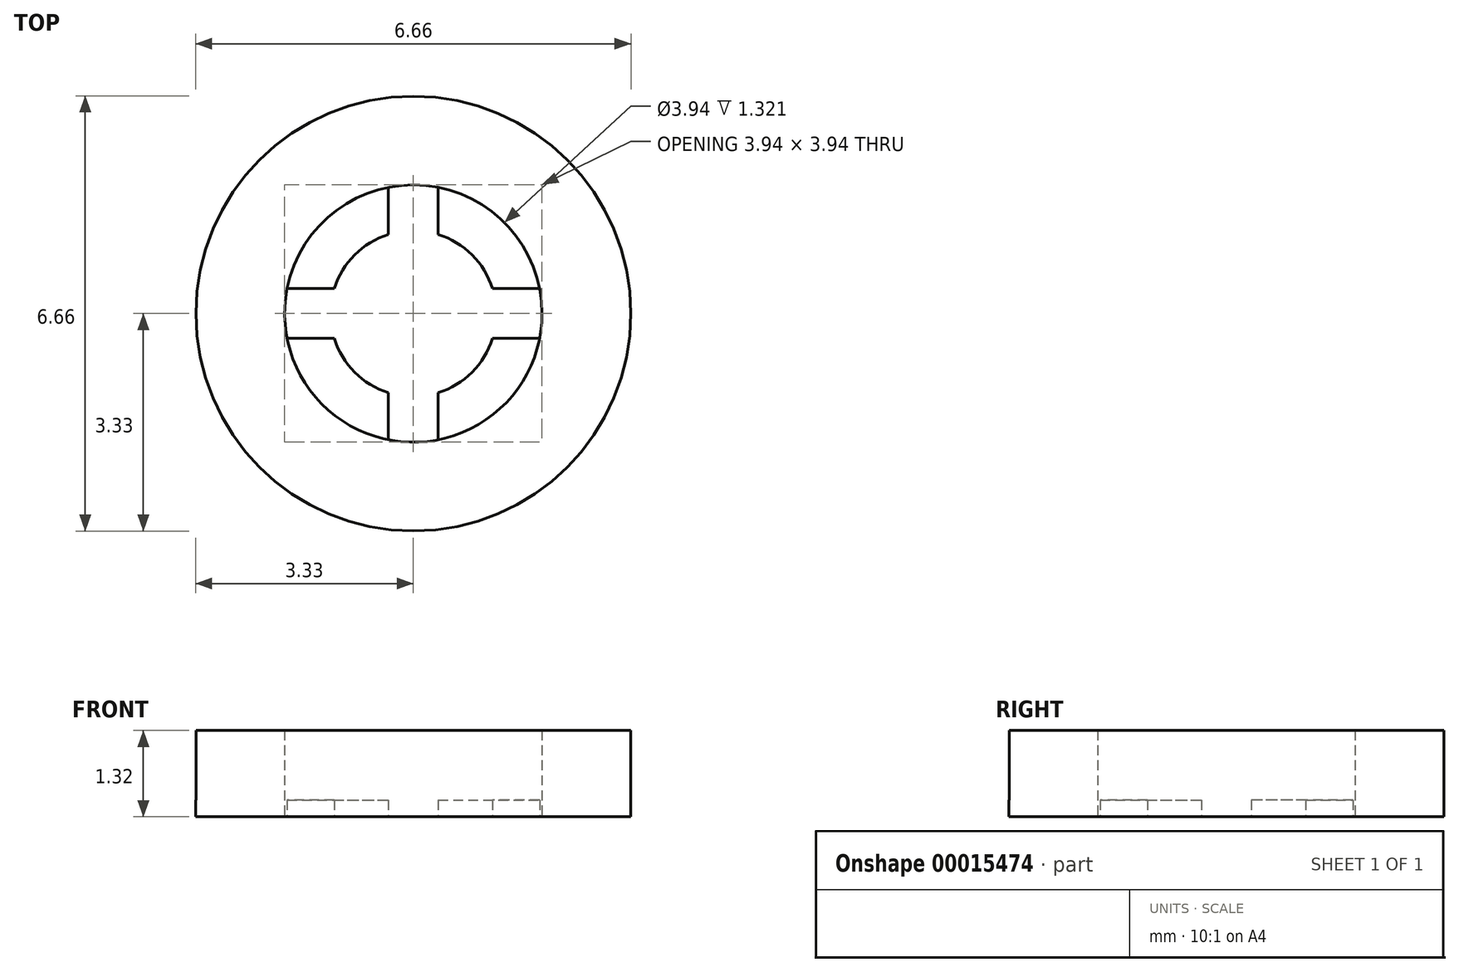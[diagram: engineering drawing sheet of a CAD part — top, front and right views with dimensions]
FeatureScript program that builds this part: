
annotation { "Feature Type Name" : "Feature", "Feature Type Description" : "" }
export const myFeature = defineFeature(function(context is Context, id is Id, definition is map)
    precondition{}
    {
        {
            var Q0;
            Q0=qCreatedBy(makeId("Top.planeOp"),FACE);
            var sketch = newSketch(context, id + "F0", { "sketchPlane" : qUnion([Q0])});
            skCircle(sketch, "E0", {"center": v(0, 0) * mm, "radius": 3.33 * mm});
            skArc(sketch, "E1", {"start": v(-1.93, 0.38) * mm, "mid": v(-1.97, 0) * mm, "end": v(-1.93, -0.38) * mm});
            skLineSegment(sketch, "E2", {"start": v(-1.97, 0) * mm, "end": v(1.97, 0) * mm, "construction": true});
            skLineSegment(sketch, "E3", {"start": v(0, 1.27) * mm, "end": v(0, -1.97) * mm, "construction": true});
            skArc(sketch, "E4", {"start": v(-0.38, 1.21) * mm, "mid": v(-0.9, 0.9) * mm, "end": v(-1.21, 0.38) * mm});
            skLineSegment(sketch, "E5", {"start": v(0.38, 1.93) * mm, "end": v(0.38, 1.21) * mm});
            skLineSegment(sketch, "E6", {"start": v(-0.38, -1.93) * mm, "end": v(-0.38, -1.21) * mm});
            skLineSegment(sketch, "E7", {"start": v(-1.93, 0.38) * mm, "end": v(-1.21, 0.38) * mm});
            skLineSegment(sketch, "E8", {"start": v(1.93, -0.38) * mm, "end": v(1.21, -0.38) * mm});
            skPoint(sketch, "E9.orphan", {"position": v(0, 1.97) * mm});
            skLineSegment(sketch, "E10.trimOffspring", {"start": v(1.21, 0.38) * mm, "end": v(1.93, 0.38) * mm});
            skLineSegment(sketch, "E11.trimOffspring", {"start": v(-0.38, 1.21) * mm, "end": v(-0.38, 1.93) * mm});
            skLineSegment(sketch, "E12.trimOffspring", {"start": v(0.38, -1.21) * mm, "end": v(0.38, -1.93) * mm});
            skArc(sketch, "E13.trimOffspring", {"start": v(1.21, 0.38) * mm, "mid": v(0.9, 0.9) * mm, "end": v(0.38, 1.21) * mm});
            skArc(sketch, "E14.trimOffspring", {"start": v(0.38, -1.21) * mm, "mid": v(0.9, -0.9) * mm, "end": v(1.21, -0.38) * mm});
            skArc(sketch, "E15.trimOffspring", {"start": v(-1.21, -0.38) * mm, "mid": v(-0.9, -0.9) * mm, "end": v(-0.38, -1.21) * mm});
            skLineSegment(sketch, "E16.trimOffspring", {"start": v(-1.21, -0.38) * mm, "end": v(-1.93, -0.38) * mm});
            skArc(sketch, "E17.trimOffspring", {"start": v(0.38, 1.93) * mm, "mid": v(0, 1.97) * mm, "end": v(-0.38, 1.93) * mm});
            skArc(sketch, "E18.trimOffspring", {"start": v(1.93, -0.38) * mm, "mid": v(1.97, 0) * mm, "end": v(1.93, 0.38) * mm});
            skArc(sketch, "E19.trimOffspring", {"start": v(-0.38, -1.93) * mm, "mid": v(0, -1.97) * mm, "end": v(0.38, -1.93) * mm});
            skSolve(sketch);
        }
        {
            var Q0;
            Q0=qSketchRegion(id+"F0",true);
            extrude(context, id + "F1", {"entities" : qUnion([Q0]), "depth" : 0.25 * mm});
        }
        {
            var Q0;
            Q0=qCreatedBy(makeId("Top.planeOp"),FACE);
            var sketch = newSketch(context, id + "F2", { "sketchPlane" : qUnion([Q0])});
            skCircle(sketch, "E20", {"center": v(0, 0) * mm, "radius": 3.33 * mm});
            skCircle(sketch, "E21", {"center": v(0, 0) * mm, "radius": 1.97 * mm});
            skSolve(sketch);
        }
        {
            var Q0;
            Q0=qSketchRegion(id+"F2",true);
            extrude(context, id + "F3", {"entities" : qUnion([Q0]), "operationType" : NewBodyOperationType.ADD, "depth" : 1.32 * mm});
        }
    });
